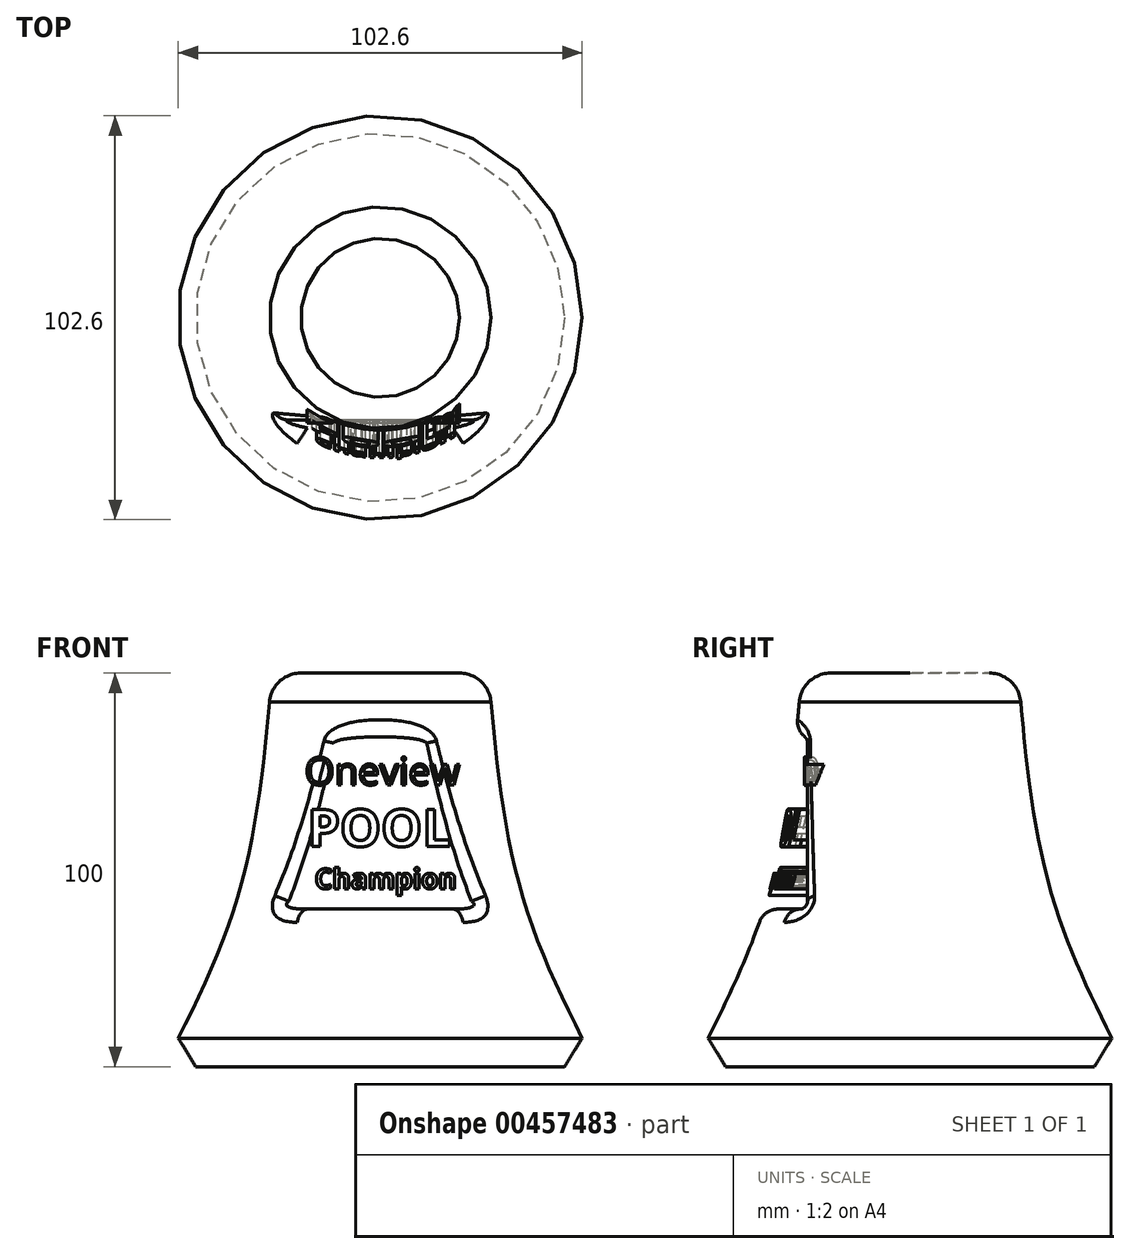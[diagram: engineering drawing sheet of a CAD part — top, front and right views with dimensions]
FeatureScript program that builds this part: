
annotation { "Feature Type Name" : "Feature", "Feature Type Description" : "" }
export const myFeature = defineFeature(function(context is Context, id is Id, definition is map)
    precondition{}
    {
        {
            var Q0;
            Q0=qCreatedBy(makeId("Top.planeOp"),FACE);
            var sketch = newSketch(context, id + "F0", { "sketchPlane" : qUnion([Q0])});
            skCircle(sketch, "E0", {"center": v(0, 0) * mm, "radius": 27.5 * mm});
            skSolve(sketch);
        }
        {
            var Q0;
            Q0=qCreatedBy(makeId("Top.planeOp"),FACE);
            cPlane(context, id + "F1", {"entities" : qUnion([Q0]), "cplaneType" : CPlaneType.OFFSET, "offset" : 100 * mm, "oppositeDirection" : true, "width" : 150 * mm, "height" : 150 * mm});
        }
        {
            var Q0;
            Q0=qCreatedBy(id+"F1.planeOp",FACE);
            var sketch = newSketch(context, id + "F2", { "sketchPlane" : qUnion([Q0])});
            skCircle(sketch, "E1", {"center": v(0, 0) * mm, "radius": 55 * mm});
            skSolve(sketch);
        }
        {
            var Q0;
            Q0=qCreatedBy(makeId("Top.planeOp"),FACE);
            cPlane(context, id + "F3", {"entities" : qUnion([Q0]), "cplaneType" : CPlaneType.OFFSET, "offset" : 60 * mm, "oppositeDirection" : true, "width" : 150 * mm, "height" : 150 * mm});
        }
        {
            var Q0;
            Q0=qCreatedBy(id+"F3.planeOp",FACE);
            var sketch = newSketch(context, id + "F4", { "sketchPlane" : qUnion([Q0])});
            skCircle(sketch, "E2", {"center": v(0, 0) * mm, "radius": 37.16 * mm});
            skSolve(sketch);
        }
        {
            var Q0;
            Q0=makeQuery(id+"F2.imprint","IMPRINT",FACE,{"disambiguationData":[TD([[makeQuery(id+"F2.imprint","IMPRINT",EDGE,{"derivedFrom":sQuery(id+"F2.wireOp",EDGE,"E1")}),1.0]])]});
            var Q1;
            Q1=makeQuery(id+"F4.imprint","IMPRINT",FACE,{"disambiguationData":[TD([[makeQuery(id+"F4.imprint","IMPRINT",EDGE,{"derivedFrom":sQuery(id+"F4.wireOp",EDGE,"E2")}),1.0]])]});
            var Q2;
            Q2=makeQuery(id+"F0.imprint","IMPRINT",FACE,{"disambiguationData":[TD([[makeQuery(id+"F0.imprint","IMPRINT",EDGE,{"derivedFrom":sQuery(id+"F0.wireOp",EDGE,"E0")}),1.0]])]});
            loft(context, id + "F5", {"sheetProfilesArray" : [{ "sheetProfileEntities" : qUnion([Q0]) }, { "sheetProfileEntities" : qUnion([Q1]) }, { "sheetProfileEntities" : qUnion([Q2]) }]});
        }
        {
            var Q0;
            Q0=qCreatedBy(makeId("Front.planeOp"),FACE);
            cPlane(context, id + "F6", {"entities" : qUnion([Q0]), "cplaneType" : CPlaneType.OFFSET, "offset" : 26 * mm, "width" : 150 * mm, "height" : 150 * mm});
        }
        {
            var Q0;
            Q0=qCreatedBy(id+"F6.planeOp",FACE);
            var sketch = newSketch(context, id + "F7", { "sketchPlane" : qUnion([Q0])});
            skLineSegment(sketch, "E3.bottom", {"start": v(-26.13, -15.77) * mm, "end": v(26.56, -15.77) * mm});
            skLineSegment(sketch, "E3.top", {"start": v(-26.13, -59.96) * mm, "end": v(26.56, -59.96) * mm});
            skLineSegment(sketch, "E3.left", {"start": v(-26.13, -15.77) * mm, "end": v(-26.13, -59.96) * mm});
            skLineSegment(sketch, "E3.right", {"start": v(26.56, -15.77) * mm, "end": v(26.56, -59.96) * mm});
            skSolve(sketch);
        }
        {
            var Q0;
            Q0 = qSketchRegion(id + "F7", true);
            extrude(context, id + "F8", {"entities" : qUnion([Q0]), "operationType" : NewBodyOperationType.REMOVE, "depth" : 25 * mm});
        }
        {
            var Q0;
            Q0=makeQuery(id+"F8.boolean.opBoolean","COPY",FACE,{"derivedFrom":makeQuery(id+"F8.opExtrude","CAP_FACE",FACE,{"disambiguationData":[OSD([sQuery(id+"F7.wireOp",EDGE,"E3.bottom"),sQuery(id+"F7.wireOp",EDGE,"E3.top"),sQuery(id+"F7.wireOp",EDGE,"E3.left"),sQuery(id+"F7.wireOp",EDGE,"E3.right")])],"isStart":true})});
            var sketch = newSketch(context, id + "F9", { "sketchPlane" : qUnion([Q0])});
            skText(sketch, "E4", { "text": "Oneview", "fontName": "OpenSans-Regular.ttf"});
            const initialGuessF9  = {"E4": [-0.01918, -0.02841, 1, 0, 0.00702]};
            skSetInitialGuess(sketch, initialGuessF9);
            skSolve(sketch);
        }
        {
            var Q0;
            Q0 = qSketchRegion(id + "F9", true);
            extrude(context, id + "F10", {"entities" : qUnion([Q0]), "operationType" : NewBodyOperationType.ADD, "oppositeDirection" : true, "depth" : 25 * mm});
        }
        {
            var Q0;
            Q0 = qSketchRegion(id + "F9", true);
            extrude(context, id + "F11", {"entities" : qUnion([Q0]), "operationType" : NewBodyOperationType.ADD, "depth" : .8 * mm});
        }
        {
            var Q0;
            Q0=makeQuery(id+"F8.boolean.opBoolean","COPY",EDGE,{"derivedFrom":makeQuery(id+"F8.opExtrude","CAP_EDGE",EDGE,{"disambiguationData":[OSD([sQuery(id+"F7.wireOp",EDGE,"E3.bottom")])],"isStart":true})});
            var Q1;
            Q1=makeQuery(id+"F8.boolean.opBoolean","COPY",EDGE,{"derivedFrom":makeQuery(id+"F8.opExtrude","CAP_EDGE",EDGE,{"disambiguationData":[OSD([sQuery(id+"F7.wireOp",EDGE,"E3.top")])],"isStart":true})});
            fillet(context, id + "F12", {"entities" : qUnion([Q0, Q1]), "radius" : 2 * mm, "tangentPropagation" : true, "allowEdgeOverflow" : false});
        }
        {
            var Q0;
            {var subQ0=sQuery(id+"F9.wireOp",EDGE,"E4.sketch_text.stroke-1");var subQ1=sQuery(id+"F9.wireOp",EDGE,"E4.sketch_text.stroke-0");var subQ2=sQuery(id+"F9.wireOp",EDGE,"E4.sketch_text.stroke-104");var subQ3=sQuery(id+"F9.wireOp",EDGE,"E4.sketch_text.stroke-6");var subQ4=sQuery(id+"F9.wireOp",EDGE,"E4.sketch_text.stroke-2");var subQ5=sQuery(id+"F9.wireOp",EDGE,"E4.sketch_text.stroke-7");var subQ6=sQuery(id+"F9.wireOp",EDGE,"E4.sketch_text.stroke-97");var subQ7=sQuery(id+"F7.wireOp",EDGE,"E3.bottom");var subQ8=sQuery(id+"F9.wireOp",EDGE,"E4.sketch_text.stroke-105");var subQ9=sQuery(id+"F7.wireOp",EDGE,"E3.left");var subQ10=sQuery(id+"F7.wireOp",EDGE,"E3.top");var subQ11=sQuery(id+"F9.wireOp",EDGE,"E4.sketch_text.stroke-99");var subQ12=sQuery(id+"F9.wireOp",EDGE,"E4.sketch_text.stroke-102");var subQ13=sQuery(id+"F9.wireOp",EDGE,"E4.sketch_text.stroke-103");var subQ14=sQuery(id+"F9.wireOp",EDGE,"E4.sketch_text.stroke-106");var subQ15=sQuery(id+"F9.wireOp",EDGE,"E4.sketch_text.stroke-98");var subQ16=sQuery(id+"F9.wireOp",EDGE,"E4.sketch_text.stroke-100");var subQ17=sQuery(id+"F9.wireOp",EDGE,"E4.sketch_text.stroke-101");Q0=makeQuery(id+"F11.boolean.opBoolean","SPLIT",FACE,{"disambiguationData":[TD([makeQuery(id+"F8.boolean.opBoolean","COPY",FACE,{"derivedFrom":makeQuery(id+"F8.opExtrude","SWEPT_FACE",FACE,{"disambiguationData":[OSD([subQ7])]})})])],"derivedFrom":makeQuery(id+"F10.boolean.opBoolean","MERGE",FACE,{"derivedFrom":[makeQuery(id+"F8.boolean.opBoolean","COPY",FACE,{"derivedFrom":makeQuery(id+"F8.opExtrude","CAP_FACE",FACE,{"disambiguationData":[OSD([subQ7,subQ10,subQ9,sQuery(id+"F7.wireOp",EDGE,"E3.right")])],"isStart":true})}),makeQuery(id+"F10.opExtrude","CAP_FACE",FACE,{"disambiguationData":[OSD([subQ1,subQ0,subQ4,sQuery(id+"F9.wireOp",EDGE,"E4.sketch_text.stroke-3"),sQuery(id+"F9.wireOp",EDGE,"E4.sketch_text.stroke-4"),sQuery(id+"F9.wireOp",EDGE,"E4.sketch_text.stroke-5"),subQ3,subQ5,sQuery(id+"F9.wireOp",EDGE,"E4.sketch_text.stroke-8"),sQuery(id+"F9.wireOp",EDGE,"E4.sketch_text.stroke-9"),sQuery(id+"F9.wireOp",EDGE,"E4.sketch_text.stroke-10"),sQuery(id+"F9.wireOp",EDGE,"E4.sketch_text.stroke-11"),sQuery(id+"F9.wireOp",EDGE,"E4.sketch_text.stroke-12"),sQuery(id+"F9.wireOp",EDGE,"E4.sketch_text.stroke-13"),sQuery(id+"F9.wireOp",EDGE,"E4.sketch_text.stroke-14"),sQuery(id+"F9.wireOp",EDGE,"E4.sketch_text.stroke-15")])],"isStart":true}),makeQuery(id+"F10.opExtrude","CAP_FACE",FACE,{"disambiguationData":[OSD([sQuery(id+"F9.wireOp",EDGE,"E4.sketch_text.stroke-93"),sQuery(id+"F9.wireOp",EDGE,"E4.sketch_text.stroke-94"),sQuery(id+"F9.wireOp",EDGE,"E4.sketch_text.stroke-95"),sQuery(id+"F9.wireOp",EDGE,"E4.sketch_text.stroke-96"),subQ6,subQ15,subQ11,subQ16,subQ17,subQ12,subQ13,subQ2,subQ8,subQ14,sQuery(id+"F9.wireOp",EDGE,"E4.sketch_text.stroke-107"),sQuery(id+"F9.wireOp",EDGE,"E4.sketch_text.stroke-108"),sQuery(id+"F9.wireOp",EDGE,"E4.sketch_text.stroke-109"),sQuery(id+"F9.wireOp",EDGE,"E4.sketch_text.stroke-110"),sQuery(id+"F9.wireOp",EDGE,"E4.sketch_text.stroke-111"),sQuery(id+"F9.wireOp",EDGE,"E4.sketch_text.stroke-112"),sQuery(id+"F9.wireOp",EDGE,"E4.sketch_text.stroke-113"),sQuery(id+"F9.wireOp",EDGE,"E4.sketch_text.stroke-114"),sQuery(id+"F9.wireOp",EDGE,"E4.sketch_text.stroke-115")])],"isStart":true})]})});}
            var sketch = newSketch(context, id + "F13", { "sketchPlane" : qUnion([Q0])});
            skText(sketch, "E5", { "text": "POOL", "fontName": "OpenSans-Bold.ttf"});
            skText(sketch, "E6", { "text": "Champion", "fontName": "OpenSans-Bold.ttf"});
            const initialGuessF13  = {"E5": [-0.0185, -0.04406, 1, 0, 0.00946], "E6": [-0.01662, -0.05479, 1, 0, 0.0051]};
            skSetInitialGuess(sketch, initialGuessF13);
            skSolve(sketch);
        }
        {
            var Q0;
            Q0 = qSketchRegion(id + "F13", true);
            var Q1;
            {var subQ23=sQuery(id+"F2.wireOp",EDGE,"E1");Q1=makeQuery(id+"F10.boolean.opBoolean","SPLIT",FACE,{"disambiguationData":[TD([makeQuery(id+"F5.opLoft","CAP_FACE",FACE,{"disambiguationData":[OSD([makeQuery(id+"F0.imprint","IMPRINT",FACE,{"disambiguationData":[TD([[makeQuery(id+"F0.imprint","IMPRINT",EDGE,{"derivedFrom":sQuery(id+"F0.wireOp",EDGE,"E0")}),1.0]])]})])],"isStart":true})])],"derivedFrom":makeQuery(id+"F5.opLoft","SWEPT_FACE",FACE,{"disambiguationData":[OSD([subQ23,sQuery(id+"F4.wireOp",EDGE,"E2")])]})});}
            var Q2;
            Q2=makeQuery(id+"F5.opLoft","SWEPT_BODY",BODY,{"disambiguationData":[OSD([makeQuery(id+"F0.imprint","IMPRINT",FACE,{"disambiguationData":[TD([[makeQuery(id+"F0.imprint","IMPRINT",EDGE,{"derivedFrom":sQuery(id+"F0.wireOp",EDGE,"E0")}),1.0]])]}),makeQuery(id+"F2.imprint","IMPRINT",FACE,{"disambiguationData":[TD([[makeQuery(id+"F2.imprint","IMPRINT",EDGE,{"derivedFrom":sQuery(id+"F2.wireOp",EDGE,"E1")}),1.0]])]}),sQuery(id+"F4.wireOp",EDGE,"E2")])]});
            extrude(context, id + "F14", {"entities" : qUnion([Q0]), "operationType" : NewBodyOperationType.ADD, "endBound" : BoundingType.UP_TO_SURFACE, "endBoundEntityFace" : qUnion([Q1]), "endBoundEntityBody" : qUnion([Q2]), "depth" : 25 * mm});
        }
        {
            var Q0;
            Q0=makeQuery(id+"F8.boolean.opBoolean","INTERSECT",EDGE,{"derivedFrom":[makeQuery(id+"F5.opLoft","SWEPT_FACE",FACE,{"disambiguationData":[OSD([sQuery(id+"F2.wireOp",EDGE,"E1"),sQuery(id+"F4.wireOp",EDGE,"E2")])]}),makeQuery(id+"F8.opExtrude","SWEPT_FACE",FACE,{"disambiguationData":[OSD([sQuery(id+"F7.wireOp",EDGE,"E3.top")])]})]});
            var Q1;
            Q1=makeQuery(id+"F8.boolean.opBoolean","INTERSECT",EDGE,{"derivedFrom":[makeQuery(id+"F5.opLoft","SWEPT_FACE",FACE,{"disambiguationData":[OSD([sQuery(id+"F2.wireOp",EDGE,"E1"),sQuery(id+"F4.wireOp",EDGE,"E2")])]}),makeQuery(id+"F8.opExtrude","SWEPT_FACE",FACE,{"disambiguationData":[OSD([sQuery(id+"F7.wireOp",EDGE,"E3.bottom")])]})]});
            fillet(context, id + "F15", {"entities" : qUnion([Q0, Q1]), "radius" : 5 * mm, "tangentPropagation" : true, "allowEdgeOverflow" : false});
        }
        {
            var Q0;
            Q0=makeQuery(id+"F5.opLoft","CAP_FACE",FACE,{"disambiguationData":[OSD([makeQuery(id+"F0.imprint","IMPRINT",FACE,{"disambiguationData":[TD([[makeQuery(id+"F0.imprint","IMPRINT",EDGE,{"derivedFrom":sQuery(id+"F0.wireOp",EDGE,"E0")}),1.0]])]})])],"isStart":true});
            fillet(context, id + "F16", {"entities" : qUnion([Q0]), "radius" : 8 * mm, "tangentPropagation" : true, "allowEdgeOverflow" : false});
        }
        {
            var Q0;
            Q0=makeQuery(id+"F5.opLoft","CAP_FACE",FACE,{"disambiguationData":[OSD([makeQuery(id+"F2.imprint","IMPRINT",FACE,{"disambiguationData":[TD([[makeQuery(id+"F2.imprint","IMPRINT",EDGE,{"derivedFrom":sQuery(id+"F2.wireOp",EDGE,"E1")}),1.0]])]})])],"isStart":true});
            chamfer(context, id + "F17", {"entities" : qUnion([Q0]), "width" : 5 * mm, "tangentPropagation" : true});
        }
    });
